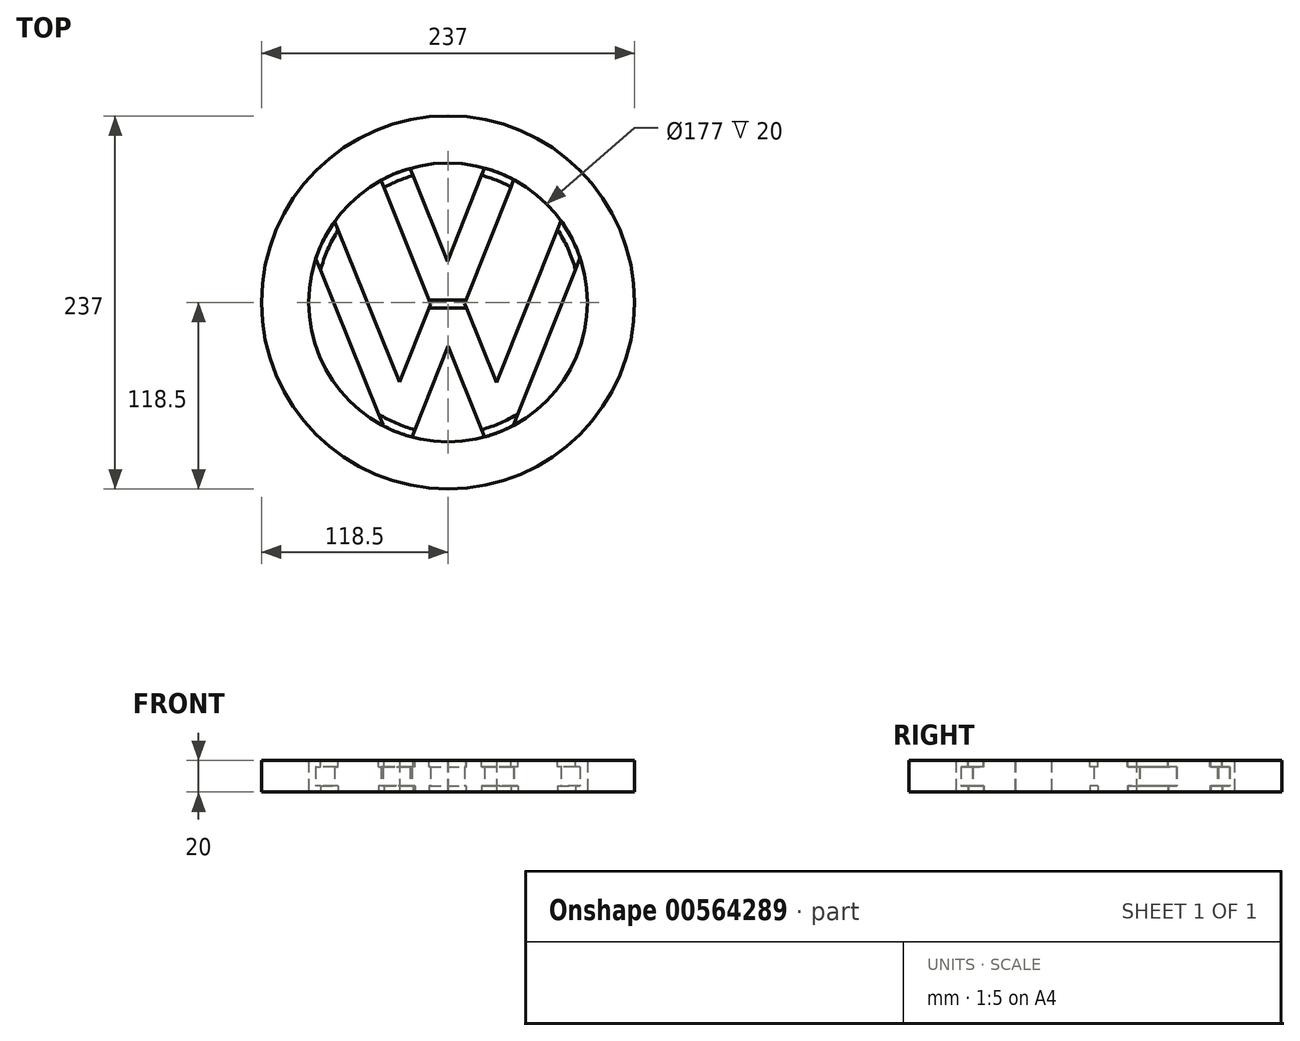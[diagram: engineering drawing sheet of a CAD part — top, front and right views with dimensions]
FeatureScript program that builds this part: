
annotation { "Feature Type Name" : "Feature", "Feature Type Description" : "" }
export const myFeature = defineFeature(function(context is Context, id is Id, definition is map)
    precondition{}
    {
        {
            var Q0;
            Q0=qCreatedBy(makeId("Top.planeOp"),FACE);
            var sketch = newSketch(context, id + "F0", { "sketchPlane" : qUnion([Q0])});
            skCircle(sketch, "E0", {"center": v(0, 0) * mm, "radius": 118.5 * mm});
            skCircle(sketch, "E1", {"center": v(0, 0) * mm, "radius": 88.5 * mm});
            skLineSegment(sketch, "E2", {"start": v(-24.16, 85.14) * mm, "end": v(41.77, -78.02) * mm});
            skLineSegment(sketch, "E3", {"start": v(-42.66, 77.54) * mm, "end": v(23.18, -85.41) * mm});
            skLineSegment(sketch, "E4", {"start": v(-33.19, 82.04) * mm, "end": v(33.12, -82.07) * mm});
            skLineSegment(sketch, "E5", {"start": v(32.66, 82.25) * mm, "end": v(-32.44, -82.34) * mm});
            skLineSegment(sketch, "E6", {"start": v(41.74, 78.04) * mm, "end": v(-22.93, -85.48) * mm});
            skLineSegment(sketch, "E7", {"start": v(23.15, 85.42) * mm, "end": v(-41.54, -78.15) * mm});
            skLineSegment(sketch, "E8", {"start": v(-88.5, 92.48) * mm, "end": v(-22.59, -70.68) * mm});
            skLineSegment(sketch, "E9", {"start": v(-107.01, 84.89) * mm, "end": v(-41.17, -78.07) * mm});
            skLineSegment(sketch, "E10", {"start": v(-97.54, 89.39) * mm, "end": v(-31.23, -74.72) * mm});
            skLineSegment(sketch, "E11", {"start": v(97.46, 89.8) * mm, "end": v(32.17, -74.72) * mm});
            skLineSegment(sketch, "E12", {"start": v(106.54, 85.56) * mm, "end": v(41.68, -77.86) * mm});
            skLineSegment(sketch, "E13", {"start": v(87.97, 92.98) * mm, "end": v(23.07, -70.55) * mm});
            skSolve(sketch);
        }
        {
            var Q0;
            Q0 = qSketchRegion(id + "F0", true);
            extrude(context, id + "F1", {"entities" : qUnion([Q0]), "depth" : 20 * mm, "offsetDistance" : 25 * mm});
        }
        {
            var Q0;
            {var subQ0=sQuery(id+"F0.wireOp",EDGE,"E1");Q0=makeQuery(id+"FmzLhq9hFsdeltd_0.boolean.opBoolean","MERGE",FACE,{"derivedFrom":[makeQuery(id+"F1.opExtrude","CAP_FACE",FACE,{"disambiguationData":[OSD([sQuery(id+"F0.wireOp",EDGE,"E0"),subQ0])],"isStart":true}),makeQuery(id+"FmzLhq9hFsdeltd_0.opExtrude","CAP_FACE",FACE,{"disambiguationData":[OSD([subQ0,sQuery(id+"F0.wireOp",EDGE,"IttgEpeb-ioXN-ueBl-Bac6-OsZWhZt1Bgas"),sQuery(id+"F0.wireOp",EDGE,"Prls1yG5-JHA4-1asJ-GGwp-gySFO1mpW6h8"),sQuery(id+"F0.wireOp",EDGE,"mh4drJd3-bM19-lmFP-MPWN-2XBcs5ePJTd2"),sQuery(id+"F0.wireOp",EDGE,"efzm9yUL-5uTw-VvDT-2yWq-ykiNYtO7lbct"),sQuery(id+"F0.wireOp",EDGE,"ySsl2yVU-FCAX-hZ6x-PiBS-Nwg2JL8P9RNb"),sQuery(id+"F0.wireOp",EDGE,"LV4Gsa3v-1TVA-SLZJ-TlKP-EnAnPvSQLPaw"),sQuery(id+"F0.wireOp",EDGE,"eli1bSyL-JAb3-BvlL-YTrB-WjPECn095AEP"),sQuery(id+"F0.wireOp",EDGE,"6QWfbkPc-qqcl-vk46-BF0k-Y0bqRtxM9o2T"),sQuery(id+"F0.wireOp",EDGE,"NsfpSdB0-OmlQ-Rh6F-cokE-o5T5V5ml29Q1"),sQuery(id+"F0.wireOp",EDGE,"NseGOavn-xDNA-WIvX-ghKd-JfhL17Lthi0D")])],"isStart":true})]});}
            var sketch = newSketch(context, id + "F2", { "sketchPlane" : qUnion([Q0])});
            skCircle(sketch, "E14", {"center": v(0, 0) * mm, "radius": 88.5 * mm});
            skCircle(sketch, "E15", {"center": v(0, 0) * mm, "radius": 83.5 * mm});
            skSolve(sketch);
        }
        {
            var Q0;
            {var subQ0=sQuery(id+"F0.wireOp",EDGE,"E7");var subQ1=sQuery(id+"F0.wireOp",EDGE,"E3");var subQ2=makeQuery(id+"F0.imprint","INTERSECT",VERTEX,{"derivedFrom":[subQ1,subQ0]});Q0=makeQuery(id+"F0.imprint","IMPRINT",FACE,{"disambiguationData":[TD([[makeQuery(id+"F0.imprint","IMPRINT",EDGE,{"disambiguationData":[TD([[subQ2,-1.0]])],"derivedFrom":subQ1}),1.0]])]});}
            var Q1;
            {var subQ0=sQuery(id+"F0.wireOp",EDGE,"E5");var subQ1=sQuery(id+"F0.wireOp",EDGE,"E3");var subQ2=makeQuery(id+"F0.imprint","INTERSECT",VERTEX,{"derivedFrom":[subQ1,subQ0]});Q1=makeQuery(id+"F0.imprint","IMPRINT",FACE,{"disambiguationData":[TD([[makeQuery(id+"F0.imprint","IMPRINT",EDGE,{"disambiguationData":[TD([[subQ2,-1.0]])],"derivedFrom":subQ1}),1.0]])]});}
            var Q2;
            {var subQ0=sQuery(id+"F0.wireOp",EDGE,"E5");var subQ1=sQuery(id+"F0.wireOp",EDGE,"E2");var subQ2=makeQuery(id+"F0.imprint","INTERSECT",VERTEX,{"derivedFrom":[subQ1,subQ0]});Q2=makeQuery(id+"F0.imprint","IMPRINT",FACE,{"disambiguationData":[TD([[makeQuery(id+"F0.imprint","IMPRINT",EDGE,{"disambiguationData":[TD([[subQ2,-1.0]])],"derivedFrom":subQ1}),-1.0]])]});}
            var Q3;
            {var subQ0=sQuery(id+"F0.wireOp",EDGE,"E7");var subQ1=sQuery(id+"F0.wireOp",EDGE,"E2");var subQ2=makeQuery(id+"F0.imprint","INTERSECT",VERTEX,{"derivedFrom":[subQ1,subQ0]});Q3=makeQuery(id+"F0.imprint","IMPRINT",FACE,{"disambiguationData":[TD([[makeQuery(id+"F0.imprint","IMPRINT",EDGE,{"disambiguationData":[TD([[subQ2,-1.0]])],"derivedFrom":subQ1}),-1.0]])]});}
            var Q4;
            {var subQ0=sQuery(id+"F0.wireOp",EDGE,"E7");var subQ1=sQuery(id+"F0.wireOp",EDGE,"E3");var subQ2=makeQuery(id+"F0.imprint","INTERSECT",VERTEX,{"derivedFrom":[subQ1,subQ0]});Q4=makeQuery(id+"F0.imprint","IMPRINT",FACE,{"disambiguationData":[TD([[makeQuery(id+"F0.imprint","IMPRINT",EDGE,{"disambiguationData":[TD([[subQ2,-1.0]])],"derivedFrom":subQ1}),-1.0]])]});}
            var Q5;
            {var subQ0=sQuery(id+"F0.wireOp",EDGE,"E5");var subQ6=sQuery(id+"F0.wireOp",EDGE,"E1");var subQ7=makeQuery(id+"F0.imprint","INTERSECT",VERTEX,{"disambiguationData":[OD(1.0)],"derivedFrom":[subQ6,subQ0]});Q5=makeQuery(id+"F0.imprint","IMPRINT",FACE,{"disambiguationData":[TD([[makeQuery(id+"F0.imprint","IMPRINT",EDGE,{"disambiguationData":[TD([[subQ7,-1.0]])],"derivedFrom":subQ6}),1.0]])]});}
            var Q6;
            {var subQ3=sQuery(id+"F0.wireOp",EDGE,"E5");var subQ4=sQuery(id+"F0.wireOp",EDGE,"E1");var subQ5=makeQuery(id+"F0.imprint","INTERSECT",VERTEX,{"disambiguationData":[OD(1.0)],"derivedFrom":[subQ4,subQ3]});Q6=makeQuery(id+"F0.imprint","IMPRINT",FACE,{"disambiguationData":[TD([[makeQuery(id+"F0.imprint","IMPRINT",EDGE,{"disambiguationData":[TD([[subQ5,1.0]])],"derivedFrom":subQ4}),1.0]])]});}
            var Q7;
            {var subQ0=sQuery(id+"F0.wireOp",EDGE,"E8");var subQ1=sQuery(id+"F0.wireOp",EDGE,"E1");var subQ2=makeQuery(id+"F0.imprint","INTERSECT",VERTEX,{"derivedFrom":[subQ1,subQ0]});Q7=makeQuery(id+"F0.imprint","IMPRINT",FACE,{"disambiguationData":[TD([[makeQuery(id+"F0.imprint","IMPRINT",EDGE,{"disambiguationData":[TD([[subQ2,-1.0]])],"derivedFrom":subQ1}),1.0]])]});}
            var Q8;
            {var subQ0=sQuery(id+"F0.wireOp",EDGE,"E10");var subQ1=sQuery(id+"F0.wireOp",EDGE,"E1");var subQ2=makeQuery(id+"F0.imprint","INTERSECT",VERTEX,{"derivedFrom":[subQ1,subQ0]});Q8=makeQuery(id+"F0.imprint","IMPRINT",FACE,{"disambiguationData":[TD([[makeQuery(id+"F0.imprint","IMPRINT",EDGE,{"disambiguationData":[TD([[subQ2,-1.0]])],"derivedFrom":subQ1}),1.0]])]});}
            var Q9;
            {var subQ0=sQuery(id+"F0.wireOp",EDGE,"E5");var subQ1=sQuery(id+"F0.wireOp",EDGE,"E1");var subQ2=makeQuery(id+"F0.imprint","INTERSECT",VERTEX,{"disambiguationData":[OD(0.0)],"derivedFrom":[subQ1,subQ0]});Q9=makeQuery(id+"F0.imprint","IMPRINT",FACE,{"disambiguationData":[TD([[makeQuery(id+"F0.imprint","IMPRINT",EDGE,{"disambiguationData":[TD([[subQ2,-1.0]])],"derivedFrom":subQ1}),1.0]])]});}
            var Q10;
            {var subQ0=sQuery(id+"F0.wireOp",EDGE,"E5");var subQ1=sQuery(id+"F0.wireOp",EDGE,"E1");var subQ2=makeQuery(id+"F0.imprint","INTERSECT",VERTEX,{"disambiguationData":[OD(0.0)],"derivedFrom":[subQ1,subQ0]});Q10=makeQuery(id+"F0.imprint","IMPRINT",FACE,{"disambiguationData":[TD([[makeQuery(id+"F0.imprint","IMPRINT",EDGE,{"disambiguationData":[TD([[subQ2,1.0]])],"derivedFrom":subQ1}),1.0]])]});}
            var Q11;
            {var subQ0=sQuery(id+"F0.wireOp",EDGE,"E3");var subQ1=sQuery(id+"F0.wireOp",EDGE,"E1");var subQ2=makeQuery(id+"F0.imprint","INTERSECT",VERTEX,{"disambiguationData":[OD(0.0)],"derivedFrom":[subQ1,subQ0]});Q11=makeQuery(id+"F0.imprint","IMPRINT",FACE,{"disambiguationData":[TD([[makeQuery(id+"F0.imprint","IMPRINT",EDGE,{"disambiguationData":[TD([[subQ2,1.0]])],"derivedFrom":subQ1}),1.0]])]});}
            var Q12;
            {var subQ0=sQuery(id+"F0.wireOp",EDGE,"E2");var subQ1=sQuery(id+"F0.wireOp",EDGE,"E1");var subQ2=makeQuery(id+"F0.imprint","INTERSECT",VERTEX,{"disambiguationData":[OD(0.0)],"derivedFrom":[subQ1,subQ0]});Q12=makeQuery(id+"F0.imprint","IMPRINT",FACE,{"disambiguationData":[TD([[makeQuery(id+"F0.imprint","IMPRINT",EDGE,{"disambiguationData":[TD([[subQ2,-1.0]])],"derivedFrom":subQ1}),1.0]])]});}
            var Q13;
            {var subQ4=sQuery(id+"F0.wireOp",EDGE,"E1");var subQ6=sQuery(id+"F0.wireOp",EDGE,"E3");var subQ7=makeQuery(id+"F0.imprint","INTERSECT",VERTEX,{"disambiguationData":[OD(1.0)],"derivedFrom":[subQ4,subQ6]});Q13=makeQuery(id+"F0.imprint","IMPRINT",FACE,{"disambiguationData":[TD([[makeQuery(id+"F0.imprint","IMPRINT",EDGE,{"disambiguationData":[TD([[subQ7,-1.0]])],"derivedFrom":subQ4}),1.0]])]});}
            var Q14;
            {var subQ0=sQuery(id+"F0.wireOp",EDGE,"E6");var subQ1=sQuery(id+"F0.wireOp",EDGE,"E2");var subQ2=makeQuery(id+"F0.imprint","INTERSECT",VERTEX,{"derivedFrom":[subQ1,subQ0]});Q14=makeQuery(id+"F0.imprint","IMPRINT",FACE,{"disambiguationData":[TD([[makeQuery(id+"F0.imprint","IMPRINT",EDGE,{"disambiguationData":[TD([[subQ2,-1.0]])],"derivedFrom":subQ1}),-1.0]])]});}
            var Q15;
            {var subQ0=sQuery(id+"F0.wireOp",EDGE,"E2");var subQ1=sQuery(id+"F0.wireOp",EDGE,"E1");var subQ2=makeQuery(id+"F0.imprint","INTERSECT",VERTEX,{"disambiguationData":[OD(1.0)],"derivedFrom":[subQ1,subQ0]});Q15=makeQuery(id+"F0.imprint","IMPRINT",FACE,{"disambiguationData":[TD([[makeQuery(id+"F0.imprint","IMPRINT",EDGE,{"disambiguationData":[TD([[subQ2,1.0]])],"derivedFrom":subQ1}),1.0]])]});}
            var Q16;
            {var subQ0=sQuery(id+"F0.wireOp",EDGE,"E11");var subQ1=sQuery(id+"F0.wireOp",EDGE,"E1");var subQ2=makeQuery(id+"F0.imprint","INTERSECT",VERTEX,{"derivedFrom":[subQ1,subQ0]});Q16=makeQuery(id+"F0.imprint","IMPRINT",FACE,{"disambiguationData":[TD([[makeQuery(id+"F0.imprint","IMPRINT",EDGE,{"disambiguationData":[TD([[subQ2,1.0]])],"derivedFrom":subQ1}),1.0]])]});}
            var Q17;
            {var subQ0=sQuery(id+"F0.wireOp",EDGE,"E11");var subQ1=sQuery(id+"F0.wireOp",EDGE,"E1");var subQ2=makeQuery(id+"F0.imprint","INTERSECT",VERTEX,{"derivedFrom":[subQ1,subQ0]});Q17=makeQuery(id+"F0.imprint","IMPRINT",FACE,{"disambiguationData":[TD([[makeQuery(id+"F0.imprint","IMPRINT",EDGE,{"disambiguationData":[TD([[subQ2,-1.0]])],"derivedFrom":subQ1}),1.0]])]});}
            extrude(context, id + "F3", {"entities" : qUnion([Q0, Q1, Q2, Q3, Q4, Q5, Q6, Q7, Q8, Q9, Q10, Q11, Q12, Q13, Q14, Q15, Q16, Q17]), "operationType" : NewBodyOperationType.ADD, "depth" : 20 * mm, "offsetDistance" : 25 * mm});
        }
        {
            var Q0;
            Q0=makeQuery(id+"F2.imprint","IMPRINT",FACE,{"disambiguationData":[TD([[makeQuery(id+"F2.imprint","IMPRINT",EDGE,{"derivedFrom":sQuery(id+"F2.wireOp",EDGE,"E14")}),-1.0]])]});
            extrude(context, id + "F4", {"entities" : qUnion([Q0]), "operationType" : NewBodyOperationType.REMOVE, "oppositeDirection" : true, "depth" : 4 * mm, "offsetDistance" : 25 * mm});
        }
        {
            var Q0;
            {var subQ0=sQuery(id+"F0.wireOp",EDGE,"E1");Q0=makeQuery(id+"F3.boolean.opBoolean","MERGE",FACE,{"derivedFrom":[makeQuery(id+"F1.opExtrude","CAP_FACE",FACE,{"disambiguationData":[OSD([sQuery(id+"F0.wireOp",EDGE,"E0"),subQ0])],"isStart":false}),makeQuery(id+"F3.opExtrude","CAP_FACE",FACE,{"disambiguationData":[OSD([subQ0,sQuery(id+"F0.wireOp",EDGE,"E2"),sQuery(id+"F0.wireOp",EDGE,"E3"),sQuery(id+"F0.wireOp",EDGE,"E6"),sQuery(id+"F0.wireOp",EDGE,"E7"),sQuery(id+"F0.wireOp",EDGE,"E8"),sQuery(id+"F0.wireOp",EDGE,"E9"),sQuery(id+"F0.wireOp",EDGE,"E12"),sQuery(id+"F0.wireOp",EDGE,"E13")])],"isStart":false})]});}
            var sketch = newSketch(context, id + "F5", { "sketchPlane" : qUnion([Q0])});
            skCircle(sketch, "E16", {"center": v(0, 0) * mm, "radius": 88.5 * mm});
            skCircle(sketch, "E17", {"center": v(0, 0) * mm, "radius": 83.5 * mm});
            skSolve(sketch);
        }
        {
            var Q0;
            {var subQ0=sQuery(id+"F5.wireOp",EDGE,"E16");var subQ1=sQuery(id+"F0.wireOp",EDGE,"E6");var subQ2=sQuery(id+"F0.wireOp",EDGE,"E1");var subQ4=makeQuery(id+"F3.opExtrude","CAP_EDGE",EDGE,{"disambiguationData":[OSD([subQ1]),TDD([makeQuery(id+"F0.imprint","IMPRINT",EDGE,{"disambiguationData":[TD([[makeQuery(id+"F0.imprint","INTERSECT",VERTEX,{"disambiguationData":[OD(0.0)],"derivedFrom":[subQ2,subQ1]}),-1.0]])],"derivedFrom":subQ1})])],"isStart":false});var subQ5=makeQuery(id+"F5.imprint","INTERSECT",VERTEX,{"derivedFrom":[subQ4,subQ0]});Q0=makeQuery(id+"F5.imprint","IMPRINT",FACE,{"disambiguationData":[TD([[makeQuery(id+"F5.imprint","IMPRINT",EDGE,{"disambiguationData":[TD([[subQ5,-1.0]])],"derivedFrom":subQ0}),1.0]])]});}
            var Q1;
            {var subQ0=sQuery(id+"F5.wireOp",EDGE,"E16");var subQ1=makeQuery(id+"F3.opExtrude","CAP_EDGE",EDGE,{"disambiguationData":[OSD([sQuery(id+"F0.wireOp",EDGE,"E12")])],"isStart":false});var subQ2=makeQuery(id+"F5.imprint","INTERSECT",VERTEX,{"derivedFrom":[subQ1,subQ0]});Q1=makeQuery(id+"F5.imprint","IMPRINT",FACE,{"disambiguationData":[TD([[makeQuery(id+"F5.imprint","IMPRINT",EDGE,{"disambiguationData":[TD([[subQ2,-1.0]])],"derivedFrom":subQ0}),1.0]])]});}
            var Q2;
            {var subQ2=sQuery(id+"F0.wireOp",EDGE,"E1");var subQ7=sQuery(id+"F0.wireOp",EDGE,"E2");var subQ9=makeQuery(id+"F3.opExtrude","CAP_EDGE",EDGE,{"disambiguationData":[OSD([subQ7]),TDD([makeQuery(id+"F0.imprint","IMPRINT",EDGE,{"disambiguationData":[TD([[makeQuery(id+"F0.imprint","INTERSECT",VERTEX,{"disambiguationData":[OD(1.0)],"derivedFrom":[subQ2,subQ7]}),1.0]])],"derivedFrom":subQ7})])],"isStart":false});Q2=makeQuery(id+"F5.imprint","IMPRINT",FACE,{"disambiguationData":[TD([[makeQuery(id+"F5.imprint","IMPRINT",EDGE,{"derivedFrom":subQ9}),-1.0]])]});}
            var Q3;
            {var subQ5=sQuery(id+"F0.wireOp",EDGE,"E1");var subQ10=sQuery(id+"F0.wireOp",EDGE,"E7");var subQ11=makeQuery(id+"F3.opExtrude","CAP_EDGE",EDGE,{"disambiguationData":[OSD([subQ10]),TDD([makeQuery(id+"F0.imprint","IMPRINT",EDGE,{"disambiguationData":[TD([[makeQuery(id+"F0.imprint","INTERSECT",VERTEX,{"disambiguationData":[OD(1.0)],"derivedFrom":[subQ5,subQ10]}),1.0]])],"derivedFrom":subQ10})])],"isStart":false});Q3=makeQuery(id+"F5.imprint","IMPRINT",FACE,{"disambiguationData":[TD([[makeQuery(id+"F5.imprint","IMPRINT",EDGE,{"derivedFrom":subQ11}),1.0]])]});}
            var Q4;
            {var subQ0=sQuery(id+"F5.wireOp",EDGE,"E16");var subQ1=makeQuery(id+"F3.opExtrude","CAP_EDGE",EDGE,{"disambiguationData":[OSD([sQuery(id+"F0.wireOp",EDGE,"E8")])],"isStart":false});var subQ2=makeQuery(id+"F5.imprint","INTERSECT",VERTEX,{"derivedFrom":[subQ1,subQ0]});Q4=makeQuery(id+"F5.imprint","IMPRINT",FACE,{"disambiguationData":[TD([[makeQuery(id+"F5.imprint","IMPRINT",EDGE,{"disambiguationData":[TD([[subQ2,-1.0]])],"derivedFrom":subQ0}),1.0]])]});}
            var Q5;
            {var subQ0=sQuery(id+"F5.wireOp",EDGE,"E16");var subQ1=sQuery(id+"F0.wireOp",EDGE,"E2");var subQ2=sQuery(id+"F0.wireOp",EDGE,"E1");var subQ4=makeQuery(id+"F3.opExtrude","CAP_EDGE",EDGE,{"disambiguationData":[OSD([subQ1]),TDD([makeQuery(id+"F0.imprint","IMPRINT",EDGE,{"disambiguationData":[TD([[makeQuery(id+"F0.imprint","INTERSECT",VERTEX,{"disambiguationData":[OD(0.0)],"derivedFrom":[subQ2,subQ1]}),-1.0]])],"derivedFrom":subQ1})])],"isStart":false});var subQ5=makeQuery(id+"F5.imprint","INTERSECT",VERTEX,{"derivedFrom":[subQ4,subQ0]});Q5=makeQuery(id+"F5.imprint","IMPRINT",FACE,{"disambiguationData":[TD([[makeQuery(id+"F5.imprint","IMPRINT",EDGE,{"disambiguationData":[TD([[subQ5,-1.0]])],"derivedFrom":subQ0}),1.0]])]});}
            extrude(context, id + "F6", {"entities" : qUnion([Q0, Q1, Q2, Q3, Q4, Q5]), "operationType" : NewBodyOperationType.REMOVE, "oppositeDirection" : true, "depth" : 4 * mm, "offsetDistance" : 25 * mm});
        }
        {
            var Q0;
            {var subQ0=sQuery(id+"F0.wireOp",EDGE,"E8");var subQ1=sQuery(id+"F0.wireOp",EDGE,"E7");var subQ2=sQuery(id+"F0.wireOp",EDGE,"E3");var subQ4=sQuery(id+"F0.wireOp",EDGE,"E1");var subQ5=sQuery(id+"F0.wireOp",EDGE,"E2");var subQ8=sQuery(id+"F0.wireOp",EDGE,"E6");var subQ13=sQuery(id+"F0.wireOp",EDGE,"E9");var subQ17=sQuery(id+"F0.wireOp",EDGE,"E12");var subQ19=sQuery(id+"F0.wireOp",EDGE,"E13");Q0=makeQuery(id+"F6.boolean.opBoolean","SPLIT",FACE,{"disambiguationData":[TD([makeQuery(id+"F3.opExtrude","SWEPT_FACE",FACE,{"disambiguationData":[OSD([subQ0])]})])],"derivedFrom":makeQuery(id+"F3.boolean.opBoolean","MERGE",FACE,{"derivedFrom":[makeQuery(id+"F1.opExtrude","CAP_FACE",FACE,{"disambiguationData":[OSD([sQuery(id+"F0.wireOp",EDGE,"E0"),subQ4])],"isStart":false}),makeQuery(id+"F3.opExtrude","CAP_FACE",FACE,{"disambiguationData":[OSD([subQ4,subQ5,subQ2,subQ8,subQ1,subQ0,subQ13,subQ17,subQ19])],"isStart":false})]})});}
            var sketch = newSketch(context, id + "F7", { "sketchPlane" : qUnion([Q0])});
            skLineSegment(sketch, "E18.bottom", {"start": v(-12.75, 1.57) * mm, "end": v(12.25, 1.57) * mm});
            skLineSegment(sketch, "E18.top", {"start": v(-12.75, -3.43) * mm, "end": v(12.25, -3.43) * mm});
            skLineSegment(sketch, "E18.left", {"start": v(-12.75, 1.57) * mm, "end": v(-12.75, -3.43) * mm});
            skLineSegment(sketch, "E18.right", {"start": v(12.25, 1.57) * mm, "end": v(12.25, -3.43) * mm});
            skSolve(sketch);
        }
        {
            var Q0;
            {var subQ0=sQuery(id+"F0.wireOp",EDGE,"E3");var subQ1=sQuery(id+"F0.wireOp",EDGE,"E1");var subQ4=makeQuery(id+"F3.opExtrude","CAP_EDGE",EDGE,{"disambiguationData":[OSD([subQ0]),TDD([makeQuery(id+"F0.imprint","IMPRINT",EDGE,{"disambiguationData":[TD([[makeQuery(id+"F0.imprint","INTERSECT",VERTEX,{"disambiguationData":[OD(0.0)],"derivedFrom":[subQ1,subQ0]}),-1.0]])],"derivedFrom":subQ0})])],"isStart":false});var subQ16=sQuery(id+"F7.wireOp",EDGE,"E18.bottom");var subQ17=makeQuery(id+"F7.imprint","INTERSECT",VERTEX,{"derivedFrom":[subQ4,subQ16]});Q0=makeQuery(id+"F7.imprint","IMPRINT",FACE,{"disambiguationData":[TD([[makeQuery(id+"F7.imprint","IMPRINT",EDGE,{"disambiguationData":[TD([[subQ17,-1.0]])],"derivedFrom":subQ16}),-1.0]])]});}
            var Q1;
            Q1=sQuery(id+"F7.wireOp",EDGE,"E18.bottom");
            var Q2;
            Q2=sQuery(id+"F7.wireOp",EDGE,"E18.top");
            var Q3;
            Q3=sQuery(id+"F7.wireOp",EDGE,"E18.right");
            var Q4;
            Q4=sQuery(id+"F7.wireOp",EDGE,"E18.left");
            extrude(context, id + "F8", {"entities" : qUnion([Q0]), "operationType" : NewBodyOperationType.REMOVE, "surfaceEntities" : qUnion([Q1, Q2, Q3, Q4]), "oppositeDirection" : true, "depth" : 4 * mm, "offsetDistance" : 25 * mm});
        }
        {
            var Q0;
            {var subQ0=sQuery(id+"F0.wireOp",EDGE,"E8");var subQ1=sQuery(id+"F0.wireOp",EDGE,"E7");var subQ2=sQuery(id+"F0.wireOp",EDGE,"E3");var subQ4=sQuery(id+"F0.wireOp",EDGE,"E1");var subQ5=sQuery(id+"F0.wireOp",EDGE,"E2");var subQ7=sQuery(id+"F0.wireOp",EDGE,"E6");var subQ10=sQuery(id+"F0.wireOp",EDGE,"E9");var subQ11=sQuery(id+"F0.wireOp",EDGE,"E13");var subQ12=sQuery(id+"F0.wireOp",EDGE,"E12");Q0=makeQuery(id+"F4.boolean.opBoolean","SPLIT",FACE,{"disambiguationData":[TD([makeQuery(id+"F3.opExtrude","SWEPT_FACE",FACE,{"disambiguationData":[OSD([subQ0])]})])],"derivedFrom":makeQuery(id+"F3.boolean.opBoolean","MERGE",FACE,{"derivedFrom":[makeQuery(id+"F1.opExtrude","CAP_FACE",FACE,{"disambiguationData":[OSD([sQuery(id+"F0.wireOp",EDGE,"E0"),subQ4])],"isStart":true}),makeQuery(id+"F3.opExtrude","CAP_FACE",FACE,{"disambiguationData":[OSD([subQ4,subQ5,subQ2,subQ7,subQ1,subQ0,subQ10,subQ12,subQ11])],"isStart":true})]})});}
            var sketch = newSketch(context, id + "F9", { "sketchPlane" : qUnion([Q0])});
            skLineSegment(sketch, "E19.bottom", {"start": v(-14.32, 3.33) * mm, "end": v(13.82, 3.33) * mm});
            skLineSegment(sketch, "E19.top", {"start": v(-14.32, -1.67) * mm, "end": v(13.82, -1.67) * mm});
            skLineSegment(sketch, "E19.left", {"start": v(-14.32, 3.33) * mm, "end": v(-14.32, -1.67) * mm});
            skLineSegment(sketch, "E19.right", {"start": v(13.82, 3.33) * mm, "end": v(13.82, -1.67) * mm});
            skSolve(sketch);
        }
        {
            var Q0;
            {var subQ0=sQuery(id+"F0.wireOp",EDGE,"E3");var subQ2=sQuery(id+"F0.wireOp",EDGE,"E7");var subQ3=makeQuery(id+"F0.imprint","INTERSECT",VERTEX,{"derivedFrom":[subQ0,subQ2]});var subQ5=makeQuery(id+"F3.opExtrude","CAP_EDGE",EDGE,{"disambiguationData":[OSD([subQ2]),TDD([makeQuery(id+"F0.imprint","IMPRINT",EDGE,{"disambiguationData":[TD([[subQ3,-1.0]])],"derivedFrom":subQ2})])],"isStart":true});var subQ7=sQuery(id+"F9.wireOp",EDGE,"E19.bottom");var subQ8=makeQuery(id+"F9.imprint","INTERSECT",VERTEX,{"derivedFrom":[subQ5,subQ7]});Q0=makeQuery(id+"F9.imprint","IMPRINT",FACE,{"disambiguationData":[TD([[makeQuery(id+"F9.imprint","IMPRINT",EDGE,{"disambiguationData":[TD([[subQ8,-1.0]])],"derivedFrom":subQ7}),-1.0]])]});}
            var Q1;
            Q1=sQuery(id+"F9.wireOp",EDGE,"E19.left");
            var Q2;
            Q2=sQuery(id+"F9.wireOp",EDGE,"E19.bottom");
            var Q3;
            Q3=sQuery(id+"F9.wireOp",EDGE,"E19.top");
            var Q4;
            Q4=sQuery(id+"F9.wireOp",EDGE,"E19.right");
            extrude(context, id + "F10", {"entities" : qUnion([Q0]), "operationType" : NewBodyOperationType.REMOVE, "surfaceEntities" : qUnion([Q1, Q2, Q3, Q4]), "oppositeDirection" : true, "depth" : 4 * mm, "offsetDistance" : 25 * mm});
        }
    });
